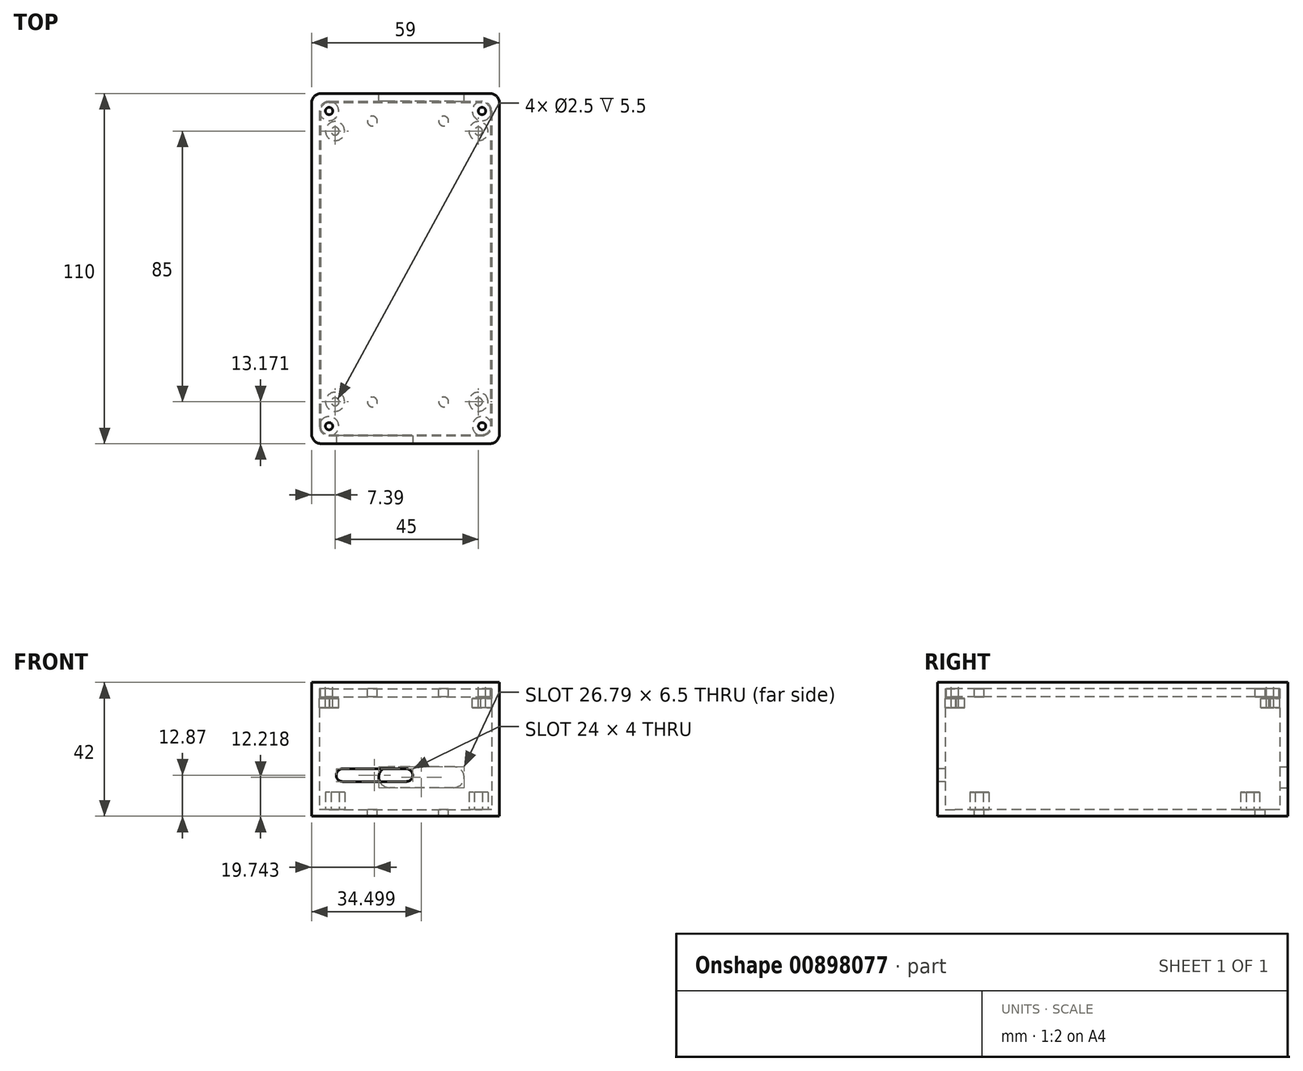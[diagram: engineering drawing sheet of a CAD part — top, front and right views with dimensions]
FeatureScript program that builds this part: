
annotation { "Feature Type Name" : "Feature", "Feature Type Description" : "" }
export const myFeature = defineFeature(function(context is Context, id is Id, definition is map)
    precondition{}
    {
        {
            var Q0;
            Q0=qCreatedBy(makeId("Top.planeOp"),FACE);
            var sketch = newSketch(context, id + "F0", { "sketchPlane" : qUnion([Q0])});
            skLineSegment(sketch, "E0.bottom", {"start": v(-45.5, 21.4) * mm, "end": v(2.5, 21.4) * mm});
            skLineSegment(sketch, "E0.top", {"start": v(-45.5, -83.6) * mm, "end": v(2.5, -83.6) * mm});
            skLineSegment(sketch, "E0.left", {"start": v(-48.5, 18.4) * mm, "end": v(-48.5, -80.6) * mm});
            skLineSegment(sketch, "E0.right", {"start": v(5.5, 18.4) * mm, "end": v(5.5, -80.6) * mm});
            skLineSegment(sketch, "E1.0", {"start": v(-48, 23.9) * mm, "end": v(5, 23.9) * mm});
            skLineSegment(sketch, "E1.1", {"start": v(-51, 20.9) * mm, "end": v(-51, -83.1) * mm});
            skLineSegment(sketch, "E1.2", {"start": v(-48, -86.1) * mm, "end": v(5, -86.1) * mm});
            skLineSegment(sketch, "E1.3", {"start": v(8, 20.9) * mm, "end": v(8, -83.1) * mm});
            skPoint(sketch, "E2.visualSharp", {"position": v(-48.5, 21.4) * mm});
            skArc(sketch, "E2.filletArc", {"start": v(-45.5, 21.4) * mm, "mid": v(-47.61, 20.53) * mm, "end": v(-48.5, 18.4) * mm});
            skPoint(sketch, "E3.visualSharp", {"position": v(-51, 23.9) * mm});
            skArc(sketch, "E3.filletArc", {"start": v(-48, 23.9) * mm, "mid": v(-50.11, 23.03) * mm, "end": v(-51, 20.9) * mm});
            skPoint(sketch, "E4.visualSharp", {"position": v(8, 23.9) * mm});
            skArc(sketch, "E4.filletArc", {"start": v(8, 20.9) * mm, "mid": v(7.13, 23.03) * mm, "end": v(5, 23.9) * mm});
            skPoint(sketch, "E5.visualSharp", {"position": v(5.5, 21.4) * mm});
            skArc(sketch, "E5.filletArc", {"start": v(5.5, 18.4) * mm, "mid": v(4.63, 20.53) * mm, "end": v(2.5, 21.4) * mm});
            skPoint(sketch, "E6.visualSharp", {"position": v(-51, -86.1) * mm});
            skArc(sketch, "E6.filletArc", {"start": v(-51, -83.1) * mm, "mid": v(-50.11, -85.21) * mm, "end": v(-48, -86.1) * mm});
            skPoint(sketch, "E7.visualSharp", {"position": v(-48.5, -83.6) * mm});
            skArc(sketch, "E7.filletArc", {"start": v(-48.5, -80.6) * mm, "mid": v(-47.61, -82.71) * mm, "end": v(-45.5, -83.6) * mm});
            skPoint(sketch, "E8.visualSharp", {"position": v(8, -86.1) * mm});
            skArc(sketch, "E8.filletArc", {"start": v(5, -86.1) * mm, "mid": v(7.13, -85.21) * mm, "end": v(8, -83.1) * mm});
            skPoint(sketch, "E9.visualSharp", {"position": v(5.5, -83.6) * mm});
            skArc(sketch, "E9.filletArc", {"start": v(2.5, -83.6) * mm, "mid": v(4.63, -82.71) * mm, "end": v(5.5, -80.6) * mm});
            skSolve(sketch);
        }
        {
            var Q0;
            Q0 = qSketchRegion(id + "F0", true);
            var Q1;
            Q1=makeQuery(id+"F0.imprint","IMPRINT",FACE,{"disambiguationData":[TD([[makeQuery(id+"F0.imprint","IMPRINT",EDGE,{"derivedFrom":sQuery(id+"F0.wireOp",EDGE,"E0.bottom")}),-1.0]])]});
            extrude(context, id + "F1", {"entities" : qUnion([Q0, Q1]), "oppositeDirection" : true, "depth" : 2 * mm, "offsetDistance" : 25 * mm});
        }
        {
            var Q0;
            Q0=makeQuery(id+"F0.imprint","IMPRINT",FACE,{"disambiguationData":[TD([[makeQuery(id+"F0.imprint","IMPRINT",EDGE,{"derivedFrom":sQuery(id+"F0.wireOp",EDGE,"E0.bottom")}),1.0]])]});
            extrude(context, id + "F2", {"entities" : qUnion([Q0]), "operationType" : NewBodyOperationType.ADD, "depth" : 38 * mm, "offsetDistance" : 25 * mm});
        }
        {
            var Q0;
            {var subQ0=sQuery(id+"F0.wireOp",EDGE,"E1.2");Q0=makeQuery(id+"F2.boolean.opBoolean","MERGE",FACE,{"derivedFrom":[makeQuery(id+"F1.opExtrude","SWEPT_FACE",FACE,{"disambiguationData":[OSD([subQ0])]}),makeQuery(id+"F2.opExtrude","SWEPT_FACE",FACE,{"disambiguationData":[OSD([subQ0])]})]});}
            var sketch = newSketch(context, id + "F3", { "sketchPlane" : qUnion([Q0])});
            skLineSegment(sketch, "E10", {"start": v(-41.25, 10.87) * mm, "end": v(-21.25, 10.87) * mm});
            skArc(sketch, "E11.0.startCap", {"start": v(-41.25, 8.87) * mm, "mid": v(-43.25, 10.87) * mm, "end": v(-41.25, 12.87) * mm});
            skArc(sketch, "E11.0.endCap", {"start": v(-21.25, 12.87) * mm, "mid": v(-19.25, 10.87) * mm, "end": v(-21.25, 8.87) * mm});
            skLineSegment(sketch, "E11.0.left", {"start": v(-41.25, 12.87) * mm, "end": v(-21.25, 12.87) * mm});
            skLineSegment(sketch, "E11.0.right", {"start": v(-41.25, 8.87) * mm, "end": v(-21.25, 8.87) * mm});
            skSolve(sketch);
        }
        {
            var Q0;
            Q0 = qSketchRegion(id + "F3", true);
            extrude(context, id + "F4", {"entities" : qUnion([Q0]), "operationType" : NewBodyOperationType.REMOVE, "oppositeDirection" : true, "depth" : 25 * mm, "offsetDistance" : 25 * mm});
        }
        {
            var Q0;
            {var subQ0=sQuery(id+"F0.wireOp",EDGE,"E1.0");Q0=makeQuery(id+"F2.boolean.opBoolean","MERGE",FACE,{"derivedFrom":[makeQuery(id+"F1.opExtrude","SWEPT_FACE",FACE,{"disambiguationData":[OSD([subQ0])]}),makeQuery(id+"F2.opExtrude","SWEPT_FACE",FACE,{"disambiguationData":[OSD([subQ0])]})]});}
            var sketch = newSketch(context, id + "F5", { "sketchPlane" : qUnion([Q0])});
            skLineSegment(sketch, "E12", {"start": v(6.35, 10.22) * mm, "end": v(26.64, 10.22) * mm});
            skArc(sketch, "E13.0.startCap", {"start": v(6.35, 6.97) * mm, "mid": v(3.1, 10.22) * mm, "end": v(6.35, 13.47) * mm});
            skArc(sketch, "E13.0.endCap", {"start": v(26.64, 13.47) * mm, "mid": v(29.89, 10.22) * mm, "end": v(26.64, 6.97) * mm});
            skLineSegment(sketch, "E13.0.left", {"start": v(6.35, 13.47) * mm, "end": v(26.64, 13.47) * mm});
            skLineSegment(sketch, "E13.0.right", {"start": v(6.35, 6.97) * mm, "end": v(26.64, 6.97) * mm});
            skSolve(sketch);
        }
        {
            var Q0;
            Q0 = qSketchRegion(id + "F5", true);
            extrude(context, id + "F6", {"entities" : qUnion([Q0]), "operationType" : NewBodyOperationType.REMOVE, "oppositeDirection" : true, "depth" : 25 * mm, "offsetDistance" : 25 * mm});
        }
        {
            var Q0;
            Q0=makeQuery(id+"F0.imprint","IMPRINT",FACE,{"disambiguationData":[TD([[makeQuery(id+"F0.imprint","IMPRINT",EDGE,{"derivedFrom":sQuery(id+"F0.wireOp",EDGE,"E0.bottom")}),-1.0]])]});
            var sketch = newSketch(context, id + "F7", { "sketchPlane" : qUnion([Q0])});
            skLineSegment(sketch, "E14.bottom", {"start": v(1.4, 12.08) * mm, "end": v(-43.6, 12.08) * mm, "construction": true});
            skLineSegment(sketch, "E14.top", {"start": v(1.4, -72.92) * mm, "end": v(-43.6, -72.92) * mm, "construction": true});
            skLineSegment(sketch, "E14.left", {"start": v(1.4, 12.08) * mm, "end": v(1.4, -72.92) * mm, "construction": true});
            skLineSegment(sketch, "E14.right", {"start": v(-43.6, 12.08) * mm, "end": v(-43.6, -72.92) * mm, "construction": true});
            skPoint(sketch, "E14.middle", {"position": v(-21.1, -30.42) * mm});
            skCircle(sketch, "E15", {"center": v(-43.6, 12.08) * mm, "radius": 3 * mm});
            skCircle(sketch, "E16", {"center": v(-43.6, 12.08) * mm, "radius": 1.25 * mm});
            skCircle(sketch, "E17", {"center": v(1.4, 12.08) * mm, "radius": 3 * mm});
            skCircle(sketch, "E18", {"center": v(1.4, 12.08) * mm, "radius": 1.25 * mm});
            skCircle(sketch, "E19", {"center": v(-43.6, -72.92) * mm, "radius": 3 * mm});
            skCircle(sketch, "E20", {"center": v(-43.6, -72.92) * mm, "radius": 1.25 * mm});
            skCircle(sketch, "E21", {"center": v(1.4, -72.92) * mm, "radius": 3 * mm});
            skCircle(sketch, "E22", {"center": v(1.4, -72.92) * mm, "radius": 1.25 * mm});
            skSolve(sketch);
        }
        {
            var Q0;
            Q0 = qSketchRegion(id + "F7", true);
            extrude(context, id + "F8", {"entities" : qUnion([Q0]), "operationType" : NewBodyOperationType.ADD, "depth" : 5.5 * mm, "offsetDistance" : 25 * mm});
        }
        {
            var Q0;
            Q0=makeQuery(id+"F2.opExtrude","CAP_FACE",FACE,{"disambiguationData":[OSD([sQuery(id+"F0.wireOp",EDGE,"E0.bottom"),sQuery(id+"F0.wireOp",EDGE,"E0.top"),sQuery(id+"F0.wireOp",EDGE,"E0.left"),sQuery(id+"F0.wireOp",EDGE,"E0.right"),sQuery(id+"F0.wireOp",EDGE,"E1.0"),sQuery(id+"F0.wireOp",EDGE,"E1.1"),sQuery(id+"F0.wireOp",EDGE,"E1.2"),sQuery(id+"F0.wireOp",EDGE,"E1.3"),sQuery(id+"F0.wireOp",EDGE,"E2.filletArc"),sQuery(id+"F0.wireOp",EDGE,"E3.filletArc"),sQuery(id+"F0.wireOp",EDGE,"E4.filletArc"),sQuery(id+"F0.wireOp",EDGE,"E5.filletArc"),sQuery(id+"F0.wireOp",EDGE,"E6.filletArc"),sQuery(id+"F0.wireOp",EDGE,"E7.filletArc"),sQuery(id+"F0.wireOp",EDGE,"E8.filletArc"),sQuery(id+"F0.wireOp",EDGE,"E9.filletArc")])],"isStart":false});
            var sketch = newSketch(context, id + "F9", { "sketchPlane" : qUnion([Q0])});
            skArc(sketch, "E23.0.0", {"start": v(-51, -83.1) * mm, "mid": v(-50.11, -85.21) * mm, "end": v(-48, -86.1) * mm});
            skLineSegment(sketch, "E23.0.1", {"start": v(-48, -86.1) * mm, "end": v(5, -86.1) * mm});
            skArc(sketch, "E23.0.2", {"start": v(5, -86.1) * mm, "mid": v(7.13, -85.21) * mm, "end": v(8, -83.1) * mm});
            skLineSegment(sketch, "E23.0.3", {"start": v(8, -83.1) * mm, "end": v(8, 20.9) * mm});
            skArc(sketch, "E23.0.4", {"start": v(8, 20.9) * mm, "mid": v(7.13, 23.03) * mm, "end": v(5, 23.9) * mm});
            skLineSegment(sketch, "E23.0.5", {"start": v(5, 23.9) * mm, "end": v(-48, 23.9) * mm});
            skArc(sketch, "E23.0.6", {"start": v(-48, 23.9) * mm, "mid": v(-50.11, 23.03) * mm, "end": v(-51, 20.9) * mm});
            skLineSegment(sketch, "E23.0.7", {"start": v(-51, 20.9) * mm, "end": v(-51, -83.1) * mm});
            skLineSegment(sketch, "E24.0", {"start": v(-48.5, 18.4) * mm, "end": v(-48.5, -80.6) * mm});
            skPoint(sketch, "E25.0", {"position": v(-47.61, -82.71) * mm});
            skLineSegment(sketch, "E26.0", {"start": v(-45.5, -83.6) * mm, "end": v(2.5, -83.6) * mm});
            skArc(sketch, "E27.0", {"start": v(-48.5, -80.6) * mm, "mid": v(-47.61, -82.71) * mm, "end": v(-45.5, -83.6) * mm});
            skArc(sketch, "E28.0", {"start": v(2.5, -83.6) * mm, "mid": v(4.63, -82.71) * mm, "end": v(5.5, -80.6) * mm});
            skLineSegment(sketch, "E29.0", {"start": v(5.5, 18.4) * mm, "end": v(5.5, -80.6) * mm});
            skArc(sketch, "E30.0", {"start": v(5.5, 18.4) * mm, "mid": v(4.63, 20.53) * mm, "end": v(2.5, 21.4) * mm});
            skLineSegment(sketch, "E31.0", {"start": v(-45.5, 21.4) * mm, "end": v(2.5, 21.4) * mm});
            skArc(sketch, "E32.0", {"start": v(-45.5, 21.4) * mm, "mid": v(-47.61, 20.53) * mm, "end": v(-48.5, 18.4) * mm});
            skArc(sketch, "E33.0", {"start": v(-45.5, 21.1) * mm, "mid": v(-47.4, 20.32) * mm, "end": v(-48.2, 18.4) * mm});
            skLineSegment(sketch, "E33.1", {"start": v(-45.5, 21.1) * mm, "end": v(2.5, 21.1) * mm});
            skLineSegment(sketch, "E33.2", {"start": v(-48.2, 18.4) * mm, "end": v(-48.2, -80.6) * mm});
            skArc(sketch, "E33.3", {"start": v(5.2, 18.4) * mm, "mid": v(4.42, 20.32) * mm, "end": v(2.5, 21.1) * mm});
            skArc(sketch, "E33.4", {"start": v(-48.2, -80.6) * mm, "mid": v(-47.4, -82.5) * mm, "end": v(-45.5, -83.3) * mm});
            skLineSegment(sketch, "E33.5", {"start": v(-45.5, -83.3) * mm, "end": v(2.5, -83.3) * mm});
            skArc(sketch, "E33.6", {"start": v(2.5, -83.3) * mm, "mid": v(4.42, -82.5) * mm, "end": v(5.2, -80.6) * mm});
            skLineSegment(sketch, "E33.7", {"start": v(5.2, 18.4) * mm, "end": v(5.2, -80.6) * mm});
            skSolve(sketch);
        }
        {
            var Q0;
            Q0=makeQuery(id+"F9.imprint","IMPRINT",FACE,{"disambiguationData":[TD([[makeQuery(id+"F9.imprint","IMPRINT",EDGE,{"derivedFrom":sQuery(id+"F9.wireOp",EDGE,"E33.0")}),1.0]])]});
            extrude(context, id + "F10", {"entities" : qUnion([Q0]), "oppositeDirection" : true, "depth" : 2.5 * mm, "offsetDistance" : 25 * mm});
        }
        {
            var Q0;
            Q0=makeQuery(id+"F9.imprint","IMPRINT",FACE,{"disambiguationData":[TD([[makeQuery(id+"F9.imprint","IMPRINT",EDGE,{"derivedFrom":sQuery(id+"F9.wireOp",EDGE,"E24.0")}),1.0]])]});
            var Q1;
            Q1=makeQuery(id+"F9.imprint","IMPRINT",FACE,{"disambiguationData":[TD([[makeQuery(id+"F9.imprint","IMPRINT",EDGE,{"derivedFrom":sQuery(id+"F9.wireOp",EDGE,"E33.0")}),1.0]])]});
            var Q2;
            Q2=makeQuery(id+"F9.imprint","IMPRINT",FACE,{"disambiguationData":[TD([[makeQuery(id+"F9.imprint","IMPRINT",EDGE,{"derivedFrom":sQuery(id+"F9.wireOp",EDGE,"E23.0.0")}),1.0]])]});
            extrude(context, id + "F11", {"entities" : qUnion([Q0, Q1, Q2]), "operationType" : NewBodyOperationType.ADD, "depth" : 2 * mm, "offsetDistance" : 25 * mm});
        }
        {
            var Q0;
            Q0=makeQuery(id+"F9.imprint","IMPRINT",FACE,{"disambiguationData":[TD([[makeQuery(id+"F9.imprint","IMPRINT",EDGE,{"derivedFrom":sQuery(id+"F9.wireOp",EDGE,"E33.0")}),1.0]])]});
            var sketch = newSketch(context, id + "F12", { "sketchPlane" : qUnion([Q0])});
            skLineSegment(sketch, "E34.bottom", {"start": v(-31.92, 15.23) * mm, "end": v(-9.52, 15.23) * mm, "construction": true});
            skLineSegment(sketch, "E34.top", {"start": v(-31.92, -72.98) * mm, "end": v(-9.52, -72.98) * mm, "construction": true});
            skLineSegment(sketch, "E34.left", {"start": v(-31.92, 15.23) * mm, "end": v(-31.92, -72.98) * mm, "construction": true});
            skLineSegment(sketch, "E34.right", {"start": v(-9.52, 15.23) * mm, "end": v(-9.52, -72.98) * mm, "construction": true});
            skCircle(sketch, "E35", {"center": v(-31.92, 15.23) * mm, "radius": 1.55 * mm});
            skCircle(sketch, "E36", {"center": v(-9.52, 15.23) * mm, "radius": 1.55 * mm});
            skCircle(sketch, "E37", {"center": v(-31.92, -72.98) * mm, "radius": 1.55 * mm});
            skCircle(sketch, "E38", {"center": v(-9.52, -72.98) * mm, "radius": 1.55 * mm});
            skSolve(sketch);
        }
        {
            var Q0;
            Q0 = qSketchRegion(id + "F12", true);
            extrude(context, id + "F13", {"entities" : qUnion([Q0]), "operationType" : NewBodyOperationType.REMOVE, "oppositeDirection" : true, "depth" : 120.8 * mm, "offsetDistance" : 25 * mm});
        }
        {
            var Q0;
            Q0=makeQuery(id+"F9.imprint","IMPRINT",FACE,{"disambiguationData":[TD([[makeQuery(id+"F9.imprint","IMPRINT",EDGE,{"derivedFrom":sQuery(id+"F9.wireOp",EDGE,"E23.0.0")}),1.0]])]});
            var sketch = newSketch(context, id + "F14", { "sketchPlane" : qUnion([Q0])});
            skLineSegment(sketch, "E39.0.0", {"start": v(-51, 20.9) * mm, "end": v(-51, -83.1) * mm});
            skArc(sketch, "E39.0.1", {"start": v(-51, -83.1) * mm, "mid": v(-50.11, -85.21) * mm, "end": v(-48, -86.1) * mm});
            skLineSegment(sketch, "E39.0.2", {"start": v(-48, -86.1) * mm, "end": v(5, -86.1) * mm});
            skArc(sketch, "E39.0.3", {"start": v(5, -86.1) * mm, "mid": v(7.13, -85.21) * mm, "end": v(8, -83.1) * mm});
            skLineSegment(sketch, "E39.0.4", {"start": v(8, -83.1) * mm, "end": v(8, 20.9) * mm});
            skArc(sketch, "E39.0.5", {"start": v(8, 20.9) * mm, "mid": v(7.13, 23.03) * mm, "end": v(5, 23.9) * mm});
            skLineSegment(sketch, "E39.0.6", {"start": v(5, 23.9) * mm, "end": v(-48, 23.9) * mm});
            skArc(sketch, "E39.0.7", {"start": v(-48, 23.9) * mm, "mid": v(-50.11, 23.03) * mm, "end": v(-51, 20.9) * mm});
            skArc(sketch, "E40.0", {"start": v(-48.5, -80.6) * mm, "mid": v(-47.61, -82.71) * mm, "end": v(-45.5, -83.6) * mm});
            skCircle(sketch, "E41", {"center": v(-45.5, -80.6) * mm, "radius": 3.01 * mm});
            skCircle(sketch, "E42", {"center": v(2.54, -80.6) * mm, "radius": 3.02 * mm});
            skArc(sketch, "E43.0", {"start": v(5.5, 18.4) * mm, "mid": v(4.63, 20.53) * mm, "end": v(2.5, 21.4) * mm});
            skArc(sketch, "E44.0", {"start": v(-45.5, 21.4) * mm, "mid": v(-47.61, 20.53) * mm, "end": v(-48.5, 18.4) * mm});
            skCircle(sketch, "E45", {"center": v(-45.5, 18.4) * mm, "radius": 3 * mm});
            skCircle(sketch, "E46", {"center": v(2.5, 18.4) * mm, "radius": 3.02 * mm});
            skCircle(sketch, "E47", {"center": v(2.54, -80.6) * mm, "radius": 1.15 * mm});
            skCircle(sketch, "E48", {"center": v(-45.5, -80.6) * mm, "radius": 1.15 * mm});
            skCircle(sketch, "E49", {"center": v(2.5, 18.4) * mm, "radius": 1.15 * mm});
            skCircle(sketch, "E50", {"center": v(-45.5, 18.4) * mm, "radius": 1.15 * mm});
            skSolve(sketch);
        }
        {
            var Q0;
            Q0=makeQuery(id+"F14.imprint","IMPRINT",FACE,{"disambiguationData":[TD([[makeQuery(id+"F14.imprint","IMPRINT",EDGE,{"derivedFrom":sQuery(id+"F14.wireOp",EDGE,"E47")}),-1.0]])]});
            var Q1;
            {var subQ0=sQuery(id+"F14.wireOp",EDGE,"E40.0");Q1=makeQuery(id+"F14.imprint","IMPRINT",FACE,{"disambiguationData":[TD([[makeQuery(id+"F14.imprint","IMPRINT",EDGE,{"derivedFrom":subQ0}),1.0]])]});}
            var Q2;
            Q2=makeQuery(id+"F14.imprint","IMPRINT",FACE,{"disambiguationData":[TD([[makeQuery(id+"F14.imprint","IMPRINT",EDGE,{"derivedFrom":sQuery(id+"F14.wireOp",EDGE,"E50")}),-1.0]])]});
            var Q3;
            {var subQ5=sQuery(id+"F14.wireOp",EDGE,"E43.0");Q3=makeQuery(id+"F14.imprint","IMPRINT",FACE,{"disambiguationData":[TD([[makeQuery(id+"F14.imprint","IMPRINT",EDGE,{"derivedFrom":subQ5}),1.0]])]});}
            extrude(context, id + "F15", {"entities" : qUnion([Q0, Q1, Q2, Q3]), "operationType" : NewBodyOperationType.ADD, "oppositeDirection" : true, "depth" : 6 * mm, "offsetDistance" : 25 * mm, "hasSecondDirection" : true, "secondDirectionOppositeDirection" : true, "secondDirectionDepth" : 3 * mm});
        }
        {
            var Q0;
            Q0=makeQuery(id+"F11.opExtrude","CAP_FACE",FACE,{"disambiguationData":[OSD([sQuery(id+"F9.wireOp",EDGE,"E23.0.0"),sQuery(id+"F9.wireOp",EDGE,"E23.0.1"),sQuery(id+"F9.wireOp",EDGE,"E23.0.2"),sQuery(id+"F9.wireOp",EDGE,"E23.0.3"),sQuery(id+"F9.wireOp",EDGE,"E23.0.4"),sQuery(id+"F9.wireOp",EDGE,"E23.0.5"),sQuery(id+"F9.wireOp",EDGE,"E23.0.6"),sQuery(id+"F9.wireOp",EDGE,"E23.0.7")])],"isStart":false});
            var sketch = newSketch(context, id + "F16", { "sketchPlane" : qUnion([Q0])});
            skCircle(sketch, "E51.0", {"center": v(2.54, -80.6) * mm, "radius": 1.15 * mm});
            skCircle(sketch, "E52.0", {"center": v(-45.5, -80.6) * mm, "radius": 1.15 * mm});
            skCircle(sketch, "E53.4", {"center": v(2.5, 18.4) * mm, "radius": 1.15 * mm});
            skCircle(sketch, "E54.0", {"center": v(-45.5, 18.4) * mm, "radius": 1.15 * mm});
            skSolve(sketch);
        }
        {
            var Q0;
            Q0 = qSketchRegion(id + "F16", true);
            extrude(context, id + "F17", {"entities" : qUnion([Q0]), "operationType" : NewBodyOperationType.REMOVE, "oppositeDirection" : true, "depth" : 25 * mm, "offsetDistance" : 25 * mm});
        }
    });
